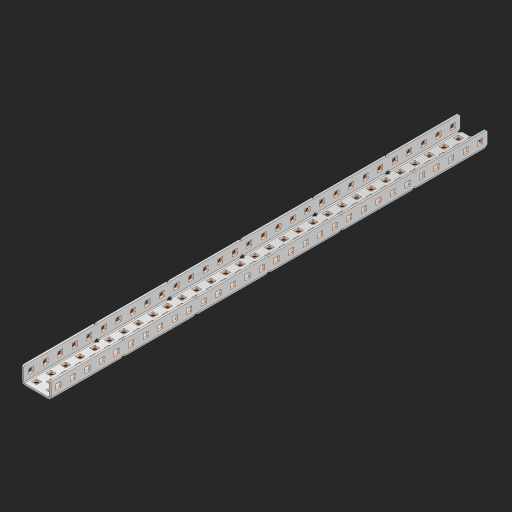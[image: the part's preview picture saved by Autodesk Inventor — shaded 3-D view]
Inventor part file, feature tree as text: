
AUTODESK INVENTOR PART (.ipt)
format: ipt  version: 2023 (Build 270158000, 158)  size: 1,861,632 bytes
history: native  units: in
note: dims shown in document units (in); Inventor stores cm internally (conversion verified against a paired STEP export)
features: other x157, extrude x148, sheet_metal_op x11, sketch x10, pattern_linear x2, mirror x1, chamfer x1
ambient origin geometry x8: Origin, YZ Plane, XZ Plane, XY Plane, X Axis, Y Axis, Z Axis, Center Point
bodies: Solid1 (feature_tree), Body (feature_tree)
feature tree (330):
  sheet_metal_op  "Flanges"
  other  "Flange Pattern Plane"
  other  "Flange Pattern Sketch"
  sheet_metal_op  "Flange Pattern"
  sheet_metal_op  "Body Pattern"
  pattern_linear  "Center Pattern"  Spacing1=0.0625in  [1 undecoded]
  other  "Arc Length"
  mirror  "Notch Mirror"
  pattern_linear  "Notch Pattern"  Spacing1=0.182in  [1 undecoded]
  chamfer  "End Chamfer"
  extrude  "Half Cut"  Depth=0.02in
  sketch  "Sketch1"  dims[d0=1.0in]
  other  "Plate1"
  sketch  "Sketch2"  dims[d1=15.0in]
  other  "Plate2"
  sheet_metal_op  "Bend1"
  sheet_metal_op  "Corner1"
  sketch  "Sketch3"  dims[d2=0.0625in]
  sketch  "Sketch7"  dims[d3=0.0625in]
  other  "Srf1"
  other  "Srf2"
  sketch  "Sketch8"  dims[d4=0.0312in]
  sketch  "Sketch9"  dims[d5=0.125in]
  other  "Srf91"
  sheet_metal_op  "Body Pattern Sketch"
  other  "Srf92"
  sketch  "Sketch13"  dims[d6=0.0625in]
  sketch  "Sketch14"  dims[d7=0.5in d8=90.0deg d9=0.0312in]
  sketch  "Sketch15"  dims[d10=0.25in]
  sketch  "Sketch16"  dims[d11=0.0625in d12=0.0625in d16=0.182in d17=0.02in d18=0.0625in d19=0.0in d20=0.25in d21=0.25in d38=11.811in d40=0.5in d41=0.7874in d43=1.0in d46=0.172in d47=1.0in d48=0.0in d49=0.182in d50=0.02in d51=0.25in d52=0.25in d53=0.0625in d54=0.0in d55=0.172in d56=1.0in d57=0.0in d58=0.25in d60=11.811in d62=0.5in d63=0.7874in d65=0.5in d85=0.1473in d86=0.1782in d88=0.04in d89=0.0625in d90=0.0in d91=0.04in d92=0.0491in d95=2.5in d96=0.04in d97=0.25in d98=45.0deg d99=0.25in d100=0.5in d101=0.0in d102=2.497in d106=0.182in d107=0.02in d108=0.5in d109=0.5in d110=0.0625in d111=0.0in d112=0.172in d113=0.5in d114=0.0in d117=0.5in d118=0.5in d119=0.5in]
  other  "Srf786"
  other  "Srf823"
  other  "Srf824"
  other  "Srf825"
  other  "Srf826"
  other  "Srf827"
  other  "Srf828"
  other  "Srf829"
  other  "Srf856"
  other  "Srf857"
  other  "Srf858"
  other  "Srf859"
  other  "Srf860"
  other  "Srf861"
  other  "Srf862"
  other  "Srf889"
  other  "Srf890"
  other  "Srf891"
  other  "Srf892"
  other  "Srf893"
  other  "Srf894"
  other  "Srf895"
  other  "Srf896"
  other  "Srf922"
  other  "Srf923"
  other  "Srf924"
  other  "Srf925"
  other  "Srf926"
  other  "Srf959"
  other  "Srf960"
  other  "Srf961"
  other  "Srf962"
  other  "Srf963"
  other  "Srf996"
  other  "Srf997"
  other  "Srf998"
  other  "Srf999"
  other  "Srf1000"
  other  "Srf1143"
  other  "Srf1144"
  other  "Srf1145"
  other  "Srf1146"
  other  "Srf1147"
  other  "Srf1148"
  other  "Srf1149"
  other  "Srf1150"
  other  "Srf1151"
  other  "Srf1152"
  other  "Srf1153"
  other  "Srf1154"
  other  "Srf1155"
  other  "Srf1156"
  other  "Srf1157"
  other  "Srf1158"
  other  "Srf1159"
  other  "Srf1160"
  other  "Srf1161"
  other  "Srf1162"
  other  "Srf1163"
  other  "Srf1164"
  other  "Srf1165"
  other  "Srf1166"
  other  "Srf1167"
  other  "Srf1168"
  other  "Srf1169"
  other  "Srf1170"
  other  "Srf1171"
  other  "Srf1172"
  other  "Srf1173"
  other  "Srf1174"
  other  "Srf1175"
  other  "Srf1176"
  other  "Srf1177"
  other  "Srf1178"
  other  "Srf1179"
  other  "Srf1180"
  other  "Srf1181"
  other  "Srf1182"
  other  "Srf1183"
  other  "Srf1184"
  other  "Srf1185"
  other  "Srf1186"
  other  "Srf1187"
  other  "Srf1188"
  other  "Srf1199"
  other  "Srf1200"
  other  "Srf1201"
  other  "Srf1202"
  other  "Srf1203"
  other  "Srf1204"
  other  "Srf1205"
  other  "Srf1206"
  other  "Srf1207"
  other  "Srf1208"
  other  "Srf1209"
  other  "Srf1210"
  other  "Srf1211"
  other  "Srf1212"
  other  "Srf1213"
  other  "Srf1214"
  other  "Srf1215"
  other  "Srf1216"
  other  "Srf1217"
  other  "Srf1218"
  other  "Srf1219"
  other  "Srf1220"
  other  "Srf1221"
  other  "Srf1222"
  other  "Srf1223"
  other  "Srf1224"
  other  "Srf1225"
  other  "Srf1226"
  other  "Srf1227"
  other  "Srf1228"
  other  "Srf1229"
  other  "Srf1230"
  other  "Srf1231"
  other  "Srf1232"
  other  "Srf1233"
  other  "Srf1234"
  other  "Srf1235"
  other  "Srf1236"
  other  "Srf1237"
  other  "Srf1238"
  other  "Srf1239"
  other  "Srf1240"
  other  "Srf1241"
  other  "Srf1242"
  other  "Srf1243"
  other  "Srf1244"
  other  "Srf1255"
  other  "Srf1256"
  other  "Srf1257"
  other  "Srf1258"
  other  "Srf1259"
  other  "Srf1260"
  other  "Srf1261"
  other  "Srf1262"
  other  "Srf1263"
  other  "Srf1264"
  other  "Srf1265"
  other  "Srf1266"
  other  "Srf1267"
  other  "Srf1268"
  other  "Srf1269"
  other  "Srf1270"
  sheet_metal_op  "Flange Stamp"
  sheet_metal_op  "Flange Circle"
  sheet_metal_op  "Body Stamp"
  sheet_metal_op  "Body Circle"
  other  "Center Stamp"
  other  "Center Circle"
  sheet_metal_op  "Notch"
  extrude  "ExtrusionSrf2"  Depth=0.0625in
  extrude  "ExtrusionSrf92"  TaperAngle=0.0deg  [1 undecoded]
  extrude  "ExtrusionSrf823"  Depth=0.5in
  extrude  "ExtrusionSrf824"  Depth=0.5in
  extrude  "ExtrusionSrf825"  Depth=0.5in
  extrude  "ExtrusionSrf826"  Depth=0.5in
  extrude  "ExtrusionSrf827"  Depth=1.0in TaperAngle=0.0deg
  extrude  "ExtrusionSrf828"  Depth=0.5in
  extrude  "ExtrusionSrf829"  Depth=0.02in
  extrude  "ExtrusionSrf856"  Depth=0.5in
  extrude  "ExtrusionSrf857"  Depth=0.5in
  extrude  "ExtrusionSrf858"  Depth=0.0625in
  extrude  "ExtrusionSrf859"  TaperAngle=0.0deg  [1 undecoded]
  extrude  "ExtrusionSrf860"  Depth=0.5in
  extrude  "ExtrusionSrf861"  Depth=1.0in TaperAngle=0.0deg
  extrude  "ExtrusionSrf862"  Depth=0.5in
  extrude  "ExtrusionSrf889"  Depth=0.5in
  extrude  "ExtrusionSrf890"  Depth=0.5in
  extrude  "ExtrusionSrf891"  Depth=0.5in
  extrude  "ExtrusionSrf892"  Depth=0.5in
  extrude  "ExtrusionSrf893"  Depth=0.5in
  extrude  "ExtrusionSrf894"  Depth=0.0625in
  extrude  "ExtrusionSrf895"  TaperAngle=0.0deg  [1 undecoded]
  extrude  "ExtrusionSrf896"  Depth=0.5in
  extrude  "ExtrusionSrf922"  Depth=0.5in
  extrude  "ExtrusionSrf923"  Depth=2.5in
  extrude  "ExtrusionSrf924"  Depth=0.5in TaperAngle=45.0deg
  extrude  "ExtrusionSrf925"  Depth=0.5in
  extrude  "ExtrusionSrf926"  Depth=0.5in TaperAngle=0.0deg
  extrude  "ExtrusionSrf959"  Depth=0.5in
  extrude  "ExtrusionSrf960"  Depth=0.5in
  extrude  "ExtrusionSrf961"  Depth=0.02in
  extrude  "ExtrusionSrf962"  Depth=0.5in
  extrude  "ExtrusionSrf963"  Depth=0.5in
  extrude  "ExtrusionSrf996"  Depth=0.0625in
  extrude  "ExtrusionSrf997"  TaperAngle=0.0deg  [1 undecoded]
  extrude  "ExtrusionSrf998"  Depth=0.5in
  extrude  "ExtrusionSrf999"  Depth=0.5in TaperAngle=0.0deg
  extrude  "ExtrusionSrf1000"  Depth=0.5in
  extrude  "ExtrusionSrf1143"  Depth=0.5in
  extrude  "ExtrusionSrf1144"  Depth=0.5in
  extrude  "ExtrusionSrf1145"  [1 undecoded]
  extrude  "ExtrusionSrf1146"  [1 undecoded]
  extrude  "ExtrusionSrf1147"  [1 undecoded]
  extrude  "ExtrusionSrf1148"  [1 undecoded]
  extrude  "ExtrusionSrf1149"  [1 undecoded]
  extrude  "ExtrusionSrf1150"  [1 undecoded]
  extrude  "ExtrusionSrf1151"  [1 undecoded]
  extrude  "ExtrusionSrf1152"  [1 undecoded]
  extrude  "ExtrusionSrf1153"  [1 undecoded]
  extrude  "ExtrusionSrf1154"  [1 undecoded]
  extrude  "ExtrusionSrf1155"  [1 undecoded]
  extrude  "ExtrusionSrf1156"  [1 undecoded]
  extrude  "ExtrusionSrf1157"  [1 undecoded]
  extrude  "ExtrusionSrf1158"  [1 undecoded]
  extrude  "ExtrusionSrf1159"  [1 undecoded]
  extrude  "ExtrusionSrf1160"  [1 undecoded]
  extrude  "ExtrusionSrf1161"  [1 undecoded]
  extrude  "ExtrusionSrf1162"  [1 undecoded]
  extrude  "ExtrusionSrf1163"  [1 undecoded]
  extrude  "ExtrusionSrf1164"  [1 undecoded]
  extrude  "ExtrusionSrf1165"  [1 undecoded]
  extrude  "ExtrusionSrf1166"  [1 undecoded]
  extrude  "ExtrusionSrf1167"  [1 undecoded]
  extrude  "ExtrusionSrf1168"  [1 undecoded]
  extrude  "ExtrusionSrf1169"  [1 undecoded]
  extrude  "ExtrusionSrf1170"  [1 undecoded]
  extrude  "ExtrusionSrf1171"  [1 undecoded]
  extrude  "ExtrusionSrf1172"  [1 undecoded]
  extrude  "ExtrusionSrf1173"  [1 undecoded]
  extrude  "ExtrusionSrf1174"  [1 undecoded]
  extrude  "ExtrusionSrf1175"  [1 undecoded]
  extrude  "ExtrusionSrf1176"  [1 undecoded]
  extrude  "ExtrusionSrf1177"  [1 undecoded]
  extrude  "ExtrusionSrf1178"  [1 undecoded]
  extrude  "ExtrusionSrf1179"  [1 undecoded]
  extrude  "ExtrusionSrf1180"  [1 undecoded]
  extrude  "ExtrusionSrf1181"  [1 undecoded]
  extrude  "ExtrusionSrf1182"  [1 undecoded]
  extrude  "ExtrusionSrf1183"  [1 undecoded]
  extrude  "ExtrusionSrf1184"  [1 undecoded]
  extrude  "ExtrusionSrf1185"  [1 undecoded]
  extrude  "ExtrusionSrf1186"  [1 undecoded]
  extrude  "ExtrusionSrf1187"  [1 undecoded]
  extrude  "ExtrusionSrf1188"  [1 undecoded]
  extrude  "ExtrusionSrf1199"  [1 undecoded]
  extrude  "ExtrusionSrf1200"  [1 undecoded]
  extrude  "ExtrusionSrf1201"  [1 undecoded]
  extrude  "ExtrusionSrf1202"  [1 undecoded]
  extrude  "ExtrusionSrf1203"  [1 undecoded]
  extrude  "ExtrusionSrf1204"  [1 undecoded]
  extrude  "ExtrusionSrf1205"  [1 undecoded]
  extrude  "ExtrusionSrf1206"  [1 undecoded]
  extrude  "ExtrusionSrf1207"  [1 undecoded]
  extrude  "ExtrusionSrf1208"  [1 undecoded]
  extrude  "ExtrusionSrf1209"  [1 undecoded]
  extrude  "ExtrusionSrf1210"  [1 undecoded]
  extrude  "ExtrusionSrf1211"  [1 undecoded]
  extrude  "ExtrusionSrf1212"  [1 undecoded]
  extrude  "ExtrusionSrf1213"  [1 undecoded]
  extrude  "ExtrusionSrf1214"  [1 undecoded]
  extrude  "ExtrusionSrf1215"  [1 undecoded]
  extrude  "ExtrusionSrf1216"  [1 undecoded]
  extrude  "ExtrusionSrf1217"  [1 undecoded]
  extrude  "ExtrusionSrf1218"  [1 undecoded]
  extrude  "ExtrusionSrf1219"  [1 undecoded]
  extrude  "ExtrusionSrf1220"  [1 undecoded]
  extrude  "ExtrusionSrf1221"  [1 undecoded]
  extrude  "ExtrusionSrf1222"  [1 undecoded]
  extrude  "ExtrusionSrf1223"  [1 undecoded]
  extrude  "ExtrusionSrf1224"  [1 undecoded]
  extrude  "ExtrusionSrf1225"  [1 undecoded]
  extrude  "ExtrusionSrf1226"  [1 undecoded]
  extrude  "ExtrusionSrf1227"  [1 undecoded]
  extrude  "ExtrusionSrf1228"  [1 undecoded]
  extrude  "ExtrusionSrf1229"  [1 undecoded]
  extrude  "ExtrusionSrf1230"  [1 undecoded]
  extrude  "ExtrusionSrf1231"  [1 undecoded]
  extrude  "ExtrusionSrf1232"  [1 undecoded]
  extrude  "ExtrusionSrf1233"  [1 undecoded]
  extrude  "ExtrusionSrf1234"  [1 undecoded]
  extrude  "ExtrusionSrf1235"  [1 undecoded]
  extrude  "ExtrusionSrf1236"  [1 undecoded]
  extrude  "ExtrusionSrf1237"  [1 undecoded]
  extrude  "ExtrusionSrf1238"  [1 undecoded]
  extrude  "ExtrusionSrf1239"  [1 undecoded]
  extrude  "ExtrusionSrf1240"  [1 undecoded]
  extrude  "ExtrusionSrf1241"  [1 undecoded]
  extrude  "ExtrusionSrf1242"  [1 undecoded]
  extrude  "ExtrusionSrf1243"  [1 undecoded]
  extrude  "ExtrusionSrf1244"  [1 undecoded]
  extrude  "ExtrusionSrf1255"  [1 undecoded]
  extrude  "ExtrusionSrf1256"  [1 undecoded]
  extrude  "ExtrusionSrf1257"  [1 undecoded]
  extrude  "ExtrusionSrf1258"  [1 undecoded]
  extrude  "ExtrusionSrf1259"  [1 undecoded]
  extrude  "ExtrusionSrf1260"  [1 undecoded]
  extrude  "ExtrusionSrf1261"  [1 undecoded]
  extrude  "ExtrusionSrf1262"  [1 undecoded]
  extrude  "ExtrusionSrf1263"  [1 undecoded]
  extrude  "ExtrusionSrf1264"  [1 undecoded]
  extrude  "ExtrusionSrf1265"  [1 undecoded]
  extrude  "ExtrusionSrf1266"  [1 undecoded]
  extrude  "ExtrusionSrf1267"  [1 undecoded]
  extrude  "ExtrusionSrf1268"  [1 undecoded]
  extrude  "ExtrusionSrf1269"  [1 undecoded]
  extrude  "ExtrusionSrf1270"  [1 undecoded]
note: 112 required parameter values undecoded (feature->parameter linkage not recoverable at this tier; creation-order binding heuristic only, values carry confidence <= 0.55)
